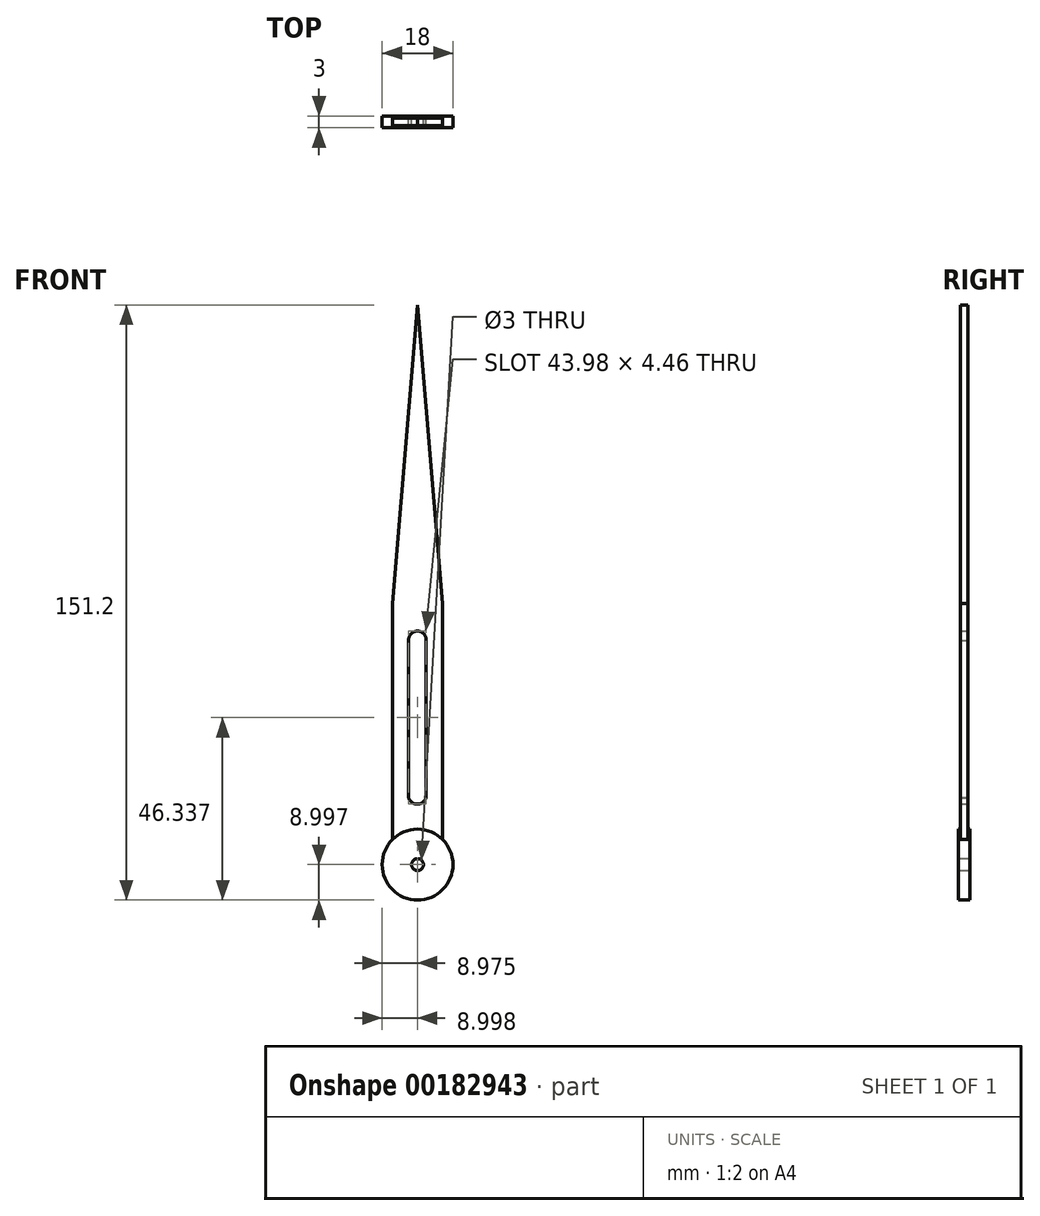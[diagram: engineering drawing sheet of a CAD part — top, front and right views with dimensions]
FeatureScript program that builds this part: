
annotation { "Feature Type Name" : "Feature", "Feature Type Description" : "" }
export const myFeature = defineFeature(function(context is Context, id is Id, definition is map)
    precondition{}
    {
        {
            var Q0;
            Q0=qCreatedBy(makeId("Front.planeOp"),FACE);
            var sketch = newSketch(context, id + "F0", { "sketchPlane" : qUnion([Q0])});
            skCircle(sketch, "E0", {"center": v(-20.04, -44.31) * mm, "radius": 1.5 * mm});
            skCircle(sketch, "E1", {"center": v(-20.04, -44.31) * mm, "radius": 9 * mm});
            skLineSegment(sketch, "E2.left", {"start": v(-26.41, -37.96) * mm, "end": v(-26.41, 22.04) * mm});
            skLineSegment(sketch, "E3", {"start": v(-26.41, 22.04) * mm, "end": v(-20.04, 97.89) * mm});
            skArc(sketch, "E4", {"start": v(-22.3, -27.34) * mm, "mid": v(-20.02, -28.97) * mm, "end": v(-17.83, -27.21) * mm});
            skArc(sketch, "E5", {"start": v(-17.83, 12.79) * mm, "mid": v(-20.13, 15.02) * mm, "end": v(-22.3, 12.66) * mm});
            skLineSegment(sketch, "E6.MirrorCS", {"start": v(-22.3, 12.66) * mm, "end": v(-22.3, -27.34) * mm});
            skLineSegment(sketch, "E7.MirrorCS", {"start": v(-13.67, 22.04) * mm, "end": v(-20.04, 97.89) * mm});
            skLineSegment(sketch, "E8.MirrorCS", {"start": v(-13.67, -37.96) * mm, "end": v(-13.67, 22.04) * mm});
            skLineSegment(sketch, "E9.MirrorCS", {"start": v(-17.83, 12.79) * mm, "end": v(-17.83, -27.21) * mm});
            skSolve(sketch);
        }
        {
            var Q0;
            Q0=makeQuery(id+"F0.imprint","IMPRINT",FACE,{"disambiguationData":[TD([[makeQuery(id+"F0.imprint","IMPRINT",EDGE,{"derivedFrom":sQuery(id+"F0.wireOp",EDGE,"E0")}),-1.0]])]});
            var Q1;
            Q1=sQuery(id+"F0.wireOp",EDGE,"p5VHldXC-XaDy-Jo6Q-gzRM-BKwmdG1nrnMR");
            var Q2;
            Q2=sQuery(id+"F0.wireOp",EDGE,"WyDkhZpA-9s04-8oUv-ohR5-d8g4u36zodpv");
            var Q3;
            Q3=sQuery(id+"F0.wireOp",EDGE,"zPygVgP6-IXea-uzZJ-7nVa-Sz4MqIU0xlYZ");
            extrude(context, id + "F1", {"entities" : qUnion([Q0]), "surfaceEntities" : qUnion([Q1, Q2, Q3]), "endBound" : BoundingType.SYMMETRIC, "depth" : 3 * mm});
        }
        {
            var Q0;
            Q0=makeQuery(id+"F0.imprint","IMPRINT",FACE,{"disambiguationData":[TD([[makeQuery(id+"F0.imprint","IMPRINT",EDGE,{"derivedFrom":sQuery(id+"F0.wireOp",EDGE,"64VVkBTR-3lK9-xNKO-ebiv-tDq6J559YHrB.left")}),-1.0]])]});
            var Q1;
            {var subQ4=sQuery(id+"F0.wireOp",EDGE,"E2.left");Q1=makeQuery(id+"F0.imprint","IMPRINT",FACE,{"disambiguationData":[TD([[makeQuery(id+"F0.imprint","IMPRINT",EDGE,{"derivedFrom":subQ4}),-1.0]])]});}
            extrude(context, id + "F2", {"entities" : qUnion([Q0, Q1]), "operationType" : NewBodyOperationType.ADD, "endBound" : BoundingType.SYMMETRIC, "depth" : 2 * mm});
        }
    });
